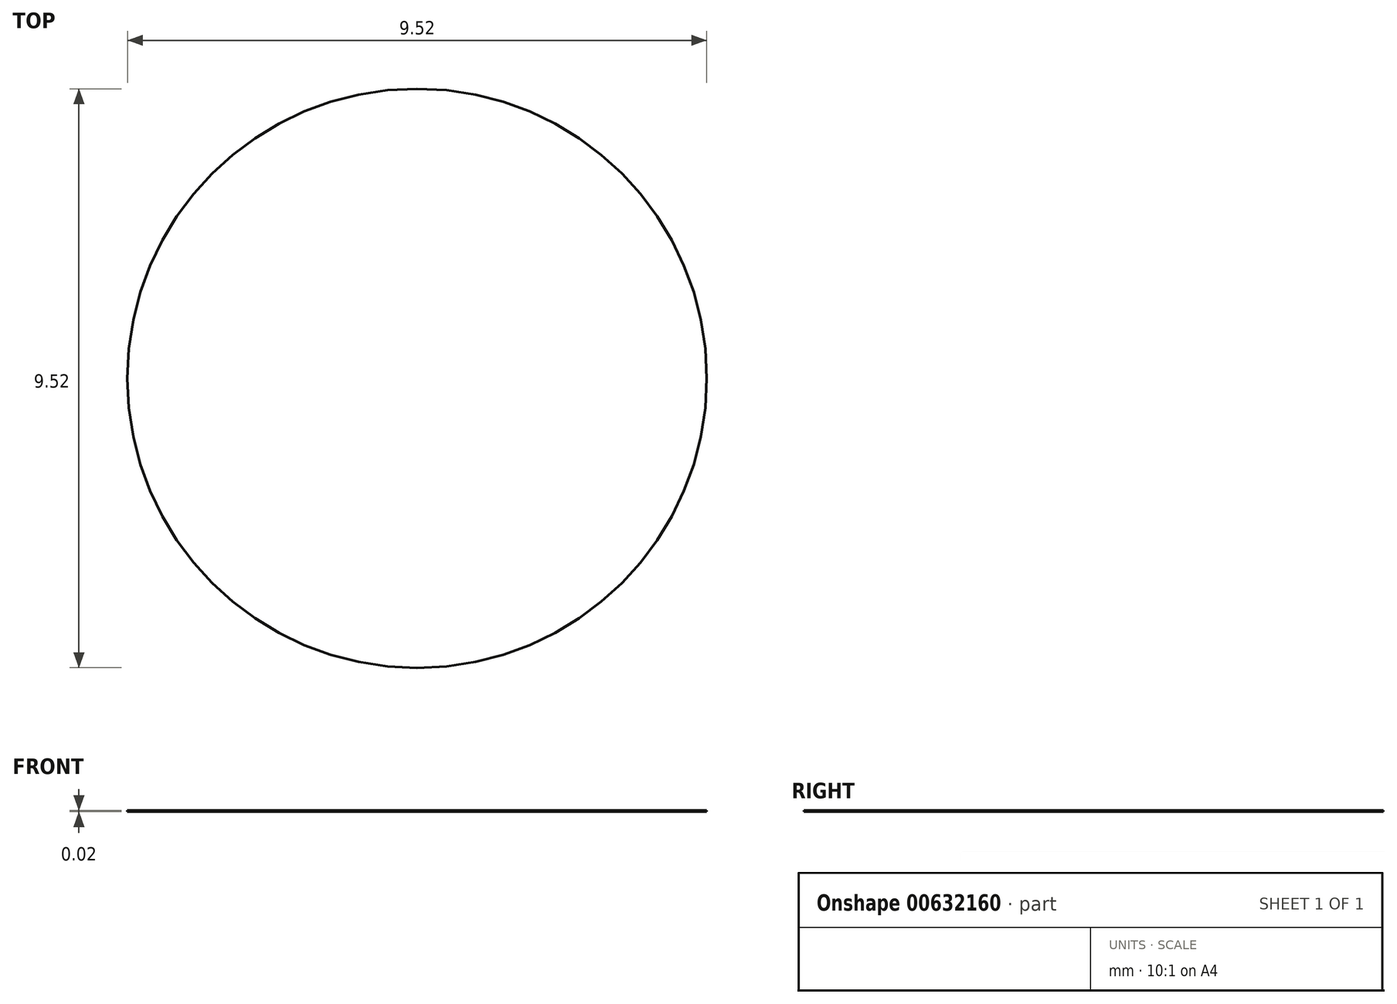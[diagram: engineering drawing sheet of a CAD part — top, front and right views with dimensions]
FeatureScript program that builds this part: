
annotation { "Feature Type Name" : "Feature", "Feature Type Description" : "" }
export const myFeature = defineFeature(function(context is Context, id is Id, definition is map)
    precondition{}
    {
        {
            var Q0;
            Q0=qCreatedBy(makeId("Top.planeOp"),FACE);
            var sketch = newSketch(context, id + "F0", { "sketchPlane" : qUnion([Q0])});
            skCircle(sketch, "E0", {"center": v(0, 0) * mm, "radius": 4.76 * mm});
            skSolve(sketch);
        }
        {
            var Q0;
            Q0 = qSketchRegion(id + "F0", true);
            extrude(context, id + "F1", {"entities" : qUnion([Q0]), "depth" : 7 / 406.4 * mm, "offsetDistance" : 25 * mm, "symmetric" : true});
        }
    });
